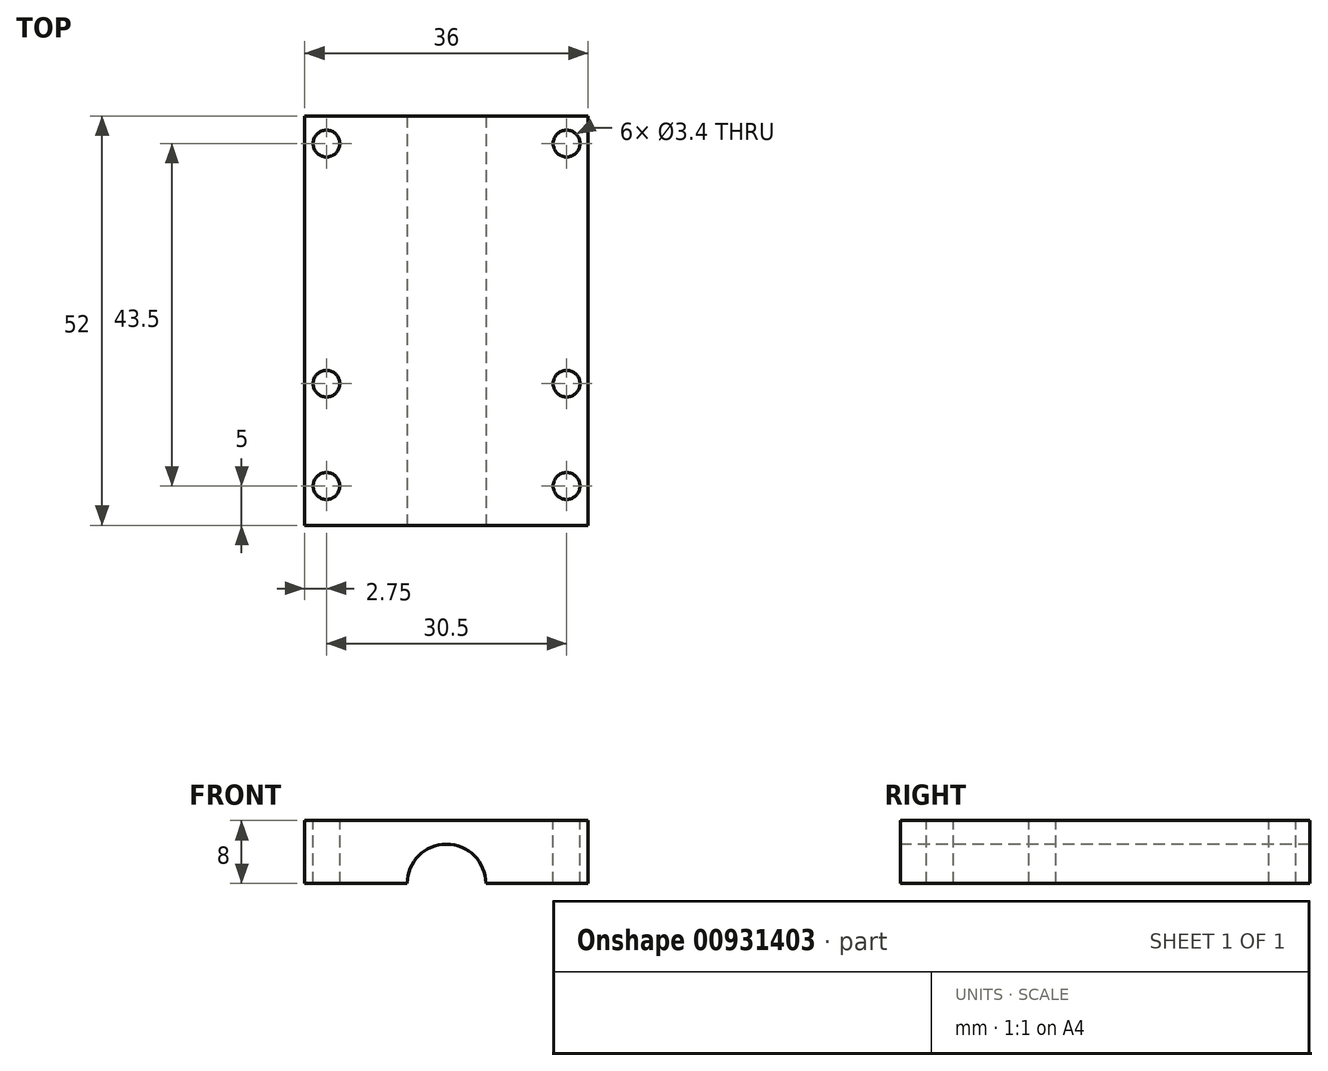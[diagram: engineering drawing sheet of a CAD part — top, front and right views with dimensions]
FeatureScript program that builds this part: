
annotation { "Feature Type Name" : "Feature", "Feature Type Description" : "" }
export const myFeature = defineFeature(function(context is Context, id is Id, definition is map)
    precondition{}
    {
        {
            var Q0;
            Q0=qCreatedBy(makeId("Top.planeOp"),FACE);
            var sketch = newSketch(context, id + "F0", { "sketchPlane" : qUnion([Q0])});
            skLineSegment(sketch, "E0.bottom", {"start": v(-18, 0) * mm, "end": v(18, 0) * mm});
            skLineSegment(sketch, "E0.top", {"start": v(-18, 52) * mm, "end": v(18, 52) * mm});
            skLineSegment(sketch, "E0.left", {"start": v(-18, 0) * mm, "end": v(-18, 52) * mm});
            skLineSegment(sketch, "E0.right", {"start": v(18, 0) * mm, "end": v(18, 52) * mm});
            skSolve(sketch);
        }
        {
            var Q0;
            Q0=makeQuery(id+"F0.imprint","IMPRINT",FACE,{"disambiguationData":[TD([[makeQuery(id+"F0.imprint","IMPRINT",EDGE,{"derivedFrom":sQuery(id+"F0.wireOp",EDGE,"E0.bottom")}),1.0]])]});
            extrude(context, id + "F1", {"entities" : qUnion([Q0]), "depth" : 8 * mm, "offsetDistance" : 25 * mm});
        }
        {
            var Q0;
            Q0=makeQuery(id+"F1.opExtrude","CAP_FACE",FACE,{"disambiguationData":[OSD([sQuery(id+"F0.wireOp",EDGE,"E0.bottom"),sQuery(id+"F0.wireOp",EDGE,"E0.top"),sQuery(id+"F0.wireOp",EDGE,"E0.left"),sQuery(id+"F0.wireOp",EDGE,"E0.right")])],"isStart":false});
            var sketch = newSketch(context, id + "F2", { "sketchPlane" : qUnion([Q0])});
            skPoint(sketch, "E1", {"position": v(15.25, 48.5) * mm});
            skPoint(sketch, "E2", {"position": v(-15.25, 48.5) * mm});
            skPoint(sketch, "E3", {"position": v(-15.25, 18) * mm});
            skPoint(sketch, "E4", {"position": v(-15.25, 5) * mm});
            skPoint(sketch, "E5", {"position": v(15.25, 5) * mm});
            skPoint(sketch, "E6", {"position": v(15.25, 18) * mm});
            skSolve(sketch);
        }
        {
            var Q0;
            Q0=sQuery(id+"F2.wireOp",VERTEX,"E1");
            var Q1;
            Q1=sQuery(id+"F2.wireOp",VERTEX,"E5");
            var Q2;
            Q2=sQuery(id+"F2.wireOp",VERTEX,"E3");
            var Q3;
            Q3=sQuery(id+"F2.wireOp",VERTEX,"E2");
            var Q4;
            Q4=sQuery(id+"F2.wireOp",VERTEX,"E6");
            var Q5;
            Q5=sQuery(id+"F2.wireOp",VERTEX,"E4");
            var Q6;
            Q6=makeQuery(id+"F1.opExtrude","SWEPT_BODY",BODY,{"disambiguationData":[OSD([sQuery(id+"F0.wireOp",EDGE,"E0.bottom"),sQuery(id+"F0.wireOp",EDGE,"E0.top"),sQuery(id+"F0.wireOp",EDGE,"E0.left"),sQuery(id+"F0.wireOp",EDGE,"E0.right")])]});
            hole(context, id + "F3", {"style" : HoleStyle.SIMPLE, "endStyle" : HoleEndStyle.THROUGH, "standardTappedOrClearance" : lookupTablePath({ "fit" : "Normal", "standard" : "ISO", "size" : "M3", "type" : "Clearance" }), "standardBlindInLast" : lookupTablePath({ "fit" : "Normal", "standard" : "ISO", "engagement" : "75%", "pitch" : "0.5 mm", "size" : "M3", "type" : "Clearance & tapped" }), "holeDiameter" : 3.4 * mm, "majorDiameter" : 5 * mm, "isTappedThrough" : true, "tappedDepth" : 12 * mm, "tapClearance" : 3, "locations" : qUnion([Q0, Q1, Q2, Q3, Q4, Q5]), "scope" : qUnion([Q6])});
        }
        {
            var Q0;
            Q0=makeQuery(id+"F1.opExtrude","SWEPT_FACE",FACE,{"disambiguationData":[OSD([sQuery(id+"F0.wireOp",EDGE,"E0.bottom")])]});
            var sketch = newSketch(context, id + "F4", { "sketchPlane" : qUnion([Q0])});
            skCircle(sketch, "E7", {"center": v(0, 0) * mm, "radius": 5 * mm});
            skSolve(sketch);
        }
        {
            var Q0;
            {var subQ0=sQuery(id+"F4.wireOp",EDGE,"E7");var subQ1=makeQuery(id+"F1.opExtrude","CAP_EDGE",EDGE,{"disambiguationData":[OSD([sQuery(id+"F0.wireOp",EDGE,"E0.bottom")])],"isStart":true});var subQ2=makeQuery(id+"F4.imprint","INTERSECT",VERTEX,{"disambiguationData":[OD(0.0)],"derivedFrom":[subQ1,subQ0]});Q0=makeQuery(id+"F4.imprint","IMPRINT",FACE,{"disambiguationData":[TD([[makeQuery(id+"F4.imprint","IMPRINT",EDGE,{"disambiguationData":[TD([[subQ2,-1.0]])],"derivedFrom":subQ0}),1.0]])]});}
            var Q1;
            {var subQ0=sQuery(id+"F4.wireOp",EDGE,"E7");var subQ1=makeQuery(id+"F1.opExtrude","CAP_EDGE",EDGE,{"disambiguationData":[OSD([sQuery(id+"F0.wireOp",EDGE,"E0.bottom")])],"isStart":true});var subQ2=makeQuery(id+"F4.imprint","INTERSECT",VERTEX,{"disambiguationData":[OD(0.0)],"derivedFrom":[subQ1,subQ0]});Q1=makeQuery(id+"F4.imprint","IMPRINT",FACE,{"disambiguationData":[TD([[makeQuery(id+"F4.imprint","IMPRINT",EDGE,{"disambiguationData":[TD([[subQ2,1.0]])],"derivedFrom":subQ0}),1.0]])]});}
            extrude(context, id + "F5", {"entities" : qUnion([Q0, Q1]), "operationType" : NewBodyOperationType.REMOVE, "endBound" : BoundingType.THROUGH_ALL, "oppositeDirection" : true, "depth" : 25 * mm, "offsetDistance" : 25 * mm});
        }
    });
